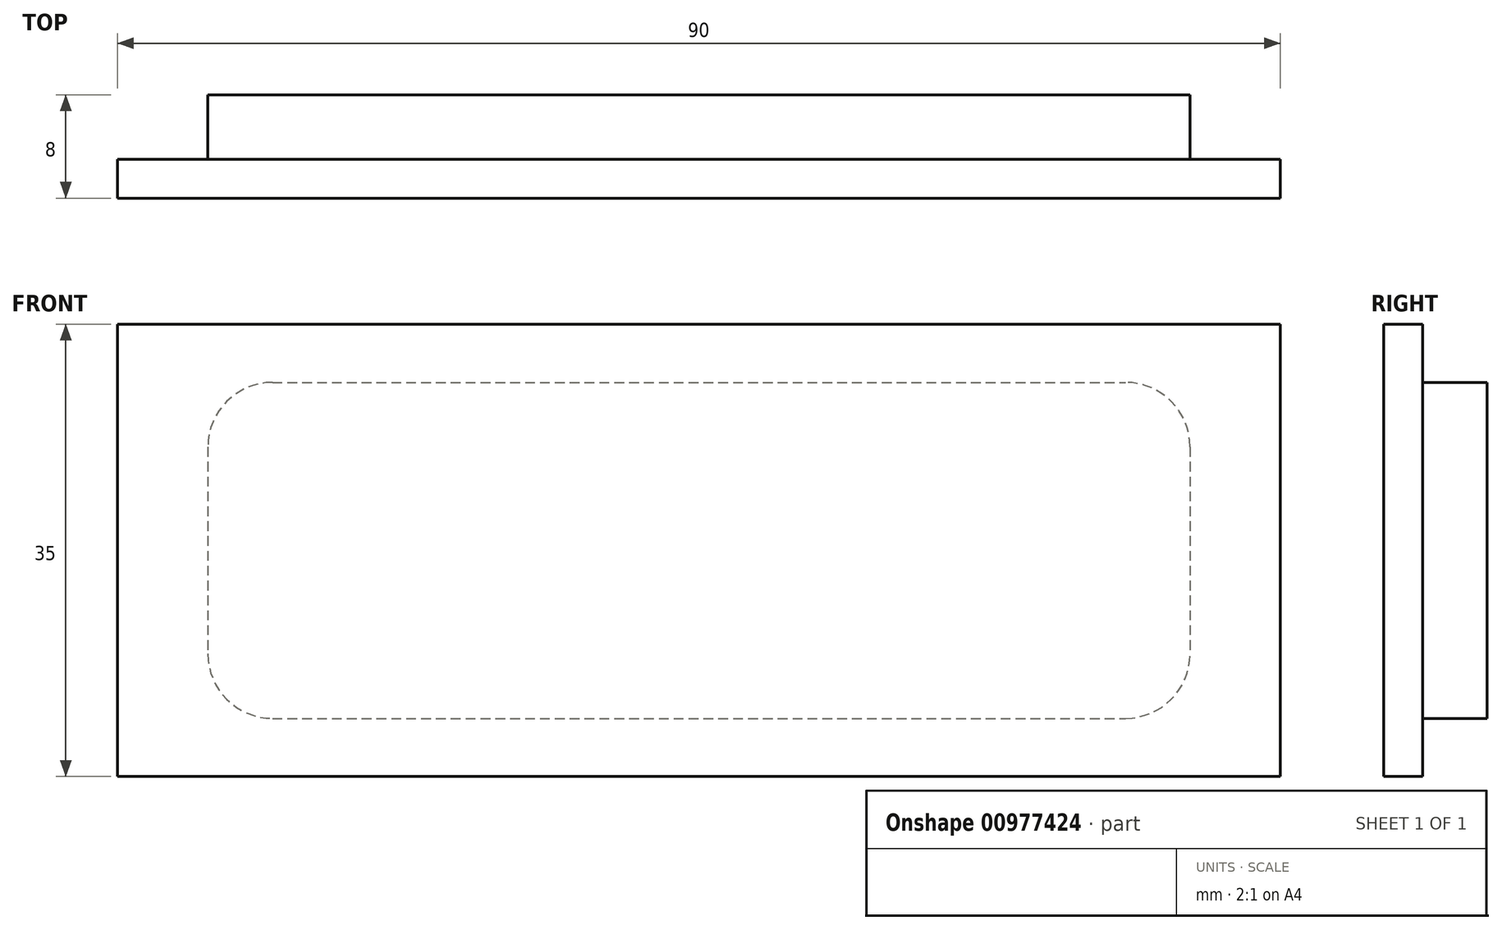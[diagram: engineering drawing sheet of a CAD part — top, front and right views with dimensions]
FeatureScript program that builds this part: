
annotation { "Feature Type Name" : "Feature", "Feature Type Description" : "" }
export const myFeature = defineFeature(function(context is Context, id is Id, definition is map)
    precondition{}
    {
        {
            var Q0;
            Q0=qCreatedBy(makeId("Front.planeOp"),FACE);
            var sketch = newSketch(context, id + "F0", { "sketchPlane" : qUnion([Q0])});
            skLineSegment(sketch, "E0.bottom", {"start": v(-38, 13) * mm, "end": v(38, 13) * mm});
            skLineSegment(sketch, "E0.top", {"start": v(-38, -13) * mm, "end": v(38, -13) * mm});
            skLineSegment(sketch, "E0.left", {"start": v(-38, 13) * mm, "end": v(-38, -13) * mm});
            skLineSegment(sketch, "E0.right", {"start": v(38, 13) * mm, "end": v(38, -13) * mm});
            skPoint(sketch, "E0.middle", {"position": v(0, 0) * mm});
            skSolve(sketch);
        }
        {
            var Q0;
            Q0=makeQuery(id+"F0.imprint","IMPRINT",FACE,{"disambiguationData":[TD([[makeQuery(id+"F0.imprint","IMPRINT",EDGE,{"derivedFrom":sQuery(id+"F0.wireOp",EDGE,"E0.bottom")}),-1.0]])]});
            extrude(context, id + "F1", {"entities" : qUnion([Q0]), "depth" : 5 * mm, "offsetDistance" : 25 * mm});
        }
        {
            var Q0;
            Q0=makeQuery(id+"F1.opExtrude","CAP_FACE",FACE,{"disambiguationData":[OSD([sQuery(id+"F0.wireOp",EDGE,"E0.bottom"),sQuery(id+"F0.wireOp",EDGE,"E0.top"),sQuery(id+"F0.wireOp",EDGE,"E0.left"),sQuery(id+"F0.wireOp",EDGE,"E0.right")])],"isStart":false});
            var sketch = newSketch(context, id + "F2", { "sketchPlane" : qUnion([Q0])});
            skLineSegment(sketch, "E1.bottom", {"start": v(-45, 17.5) * mm, "end": v(45, 17.5) * mm});
            skLineSegment(sketch, "E1.top", {"start": v(-45, -17.5) * mm, "end": v(45, -17.5) * mm});
            skLineSegment(sketch, "E1.left", {"start": v(-45, 17.5) * mm, "end": v(-45, -17.5) * mm});
            skLineSegment(sketch, "E1.right", {"start": v(45, 17.5) * mm, "end": v(45, -17.5) * mm});
            skPoint(sketch, "E1.middle", {"position": v(0, 0) * mm});
            skSolve(sketch);
        }
        {
            var Q0;
            Q0=qSketchRegion(id+"F2",true);
            extrude(context, id + "F3", {"entities" : qUnion([Q0]), "operationType" : NewBodyOperationType.ADD, "depth" : 3 * mm, "offsetDistance" : 25 * mm});
        }
        {
            var Q0;
            Q0=makeQuery(id+"F1.opExtrude","SWEPT_EDGE",EDGE,{"disambiguationData":[OSD([sQuery(id+"F0.wireOp",EDGE,"E0.bottom"),sQuery(id+"F0.wireOp",EDGE,"E0.left")])]});
            var Q1;
            Q1=makeQuery(id+"F1.opExtrude","SWEPT_EDGE",EDGE,{"disambiguationData":[OSD([sQuery(id+"F0.wireOp",EDGE,"E0.bottom"),sQuery(id+"F0.wireOp",EDGE,"E0.right")])]});
            var Q2;
            Q2=makeQuery(id+"F1.opExtrude","SWEPT_EDGE",EDGE,{"disambiguationData":[OSD([sQuery(id+"F0.wireOp",EDGE,"E0.top"),sQuery(id+"F0.wireOp",EDGE,"E0.right")])]});
            var Q3;
            Q3=makeQuery(id+"F1.opExtrude","SWEPT_EDGE",EDGE,{"disambiguationData":[OSD([sQuery(id+"F0.wireOp",EDGE,"E0.top"),sQuery(id+"F0.wireOp",EDGE,"E0.left")])]});
            fillet(context, id + "F4", {"entities" : qUnion([Q0, Q1, Q2, Q3]), "radius" : 5 * mm, "tangentPropagation" : true, "allowEdgeOverflow" : false});
        }
    });
